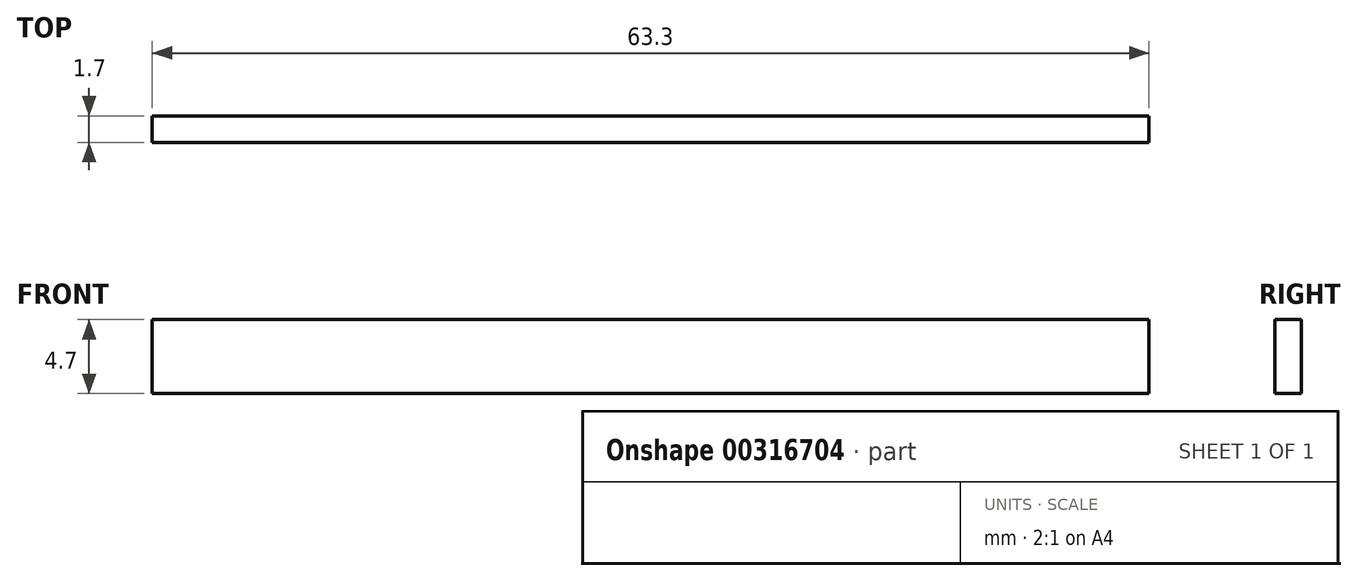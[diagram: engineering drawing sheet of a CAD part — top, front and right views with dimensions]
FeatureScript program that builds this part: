
annotation { "Feature Type Name" : "Feature", "Feature Type Description" : "" }
export const myFeature = defineFeature(function(context is Context, id is Id, definition is map)
    precondition{}
    {
        {
            var Q0;
            Q0=qCreatedBy(makeId("Front.planeOp"),FACE);
            var sketch = newSketch(context, id + "F0", { "sketchPlane" : qUnion([Q0])});
            skLineSegment(sketch, "E0.bottom", {"start": v(31.65, 2.35) * mm, "end": v(-31.65, 2.35) * mm});
            skLineSegment(sketch, "E0.top", {"start": v(31.65, -2.35) * mm, "end": v(-31.65, -2.35) * mm});
            skLineSegment(sketch, "E0.left", {"start": v(31.65, 2.35) * mm, "end": v(31.65, -2.35) * mm});
            skLineSegment(sketch, "E0.right", {"start": v(-31.65, 2.35) * mm, "end": v(-31.65, -2.35) * mm});
            skPoint(sketch, "E0.middle", {"position": v(0, 0) * mm});
            skSolve(sketch);
        }
        {
            var Q0;
            Q0 = qSketchRegion(id + "F0", true);
            extrude(context, id + "F1", {"entities" : qUnion([Q0]), "endBound" : BoundingType.SYMMETRIC, "depth" : 1.7 * mm});
        }
    });
